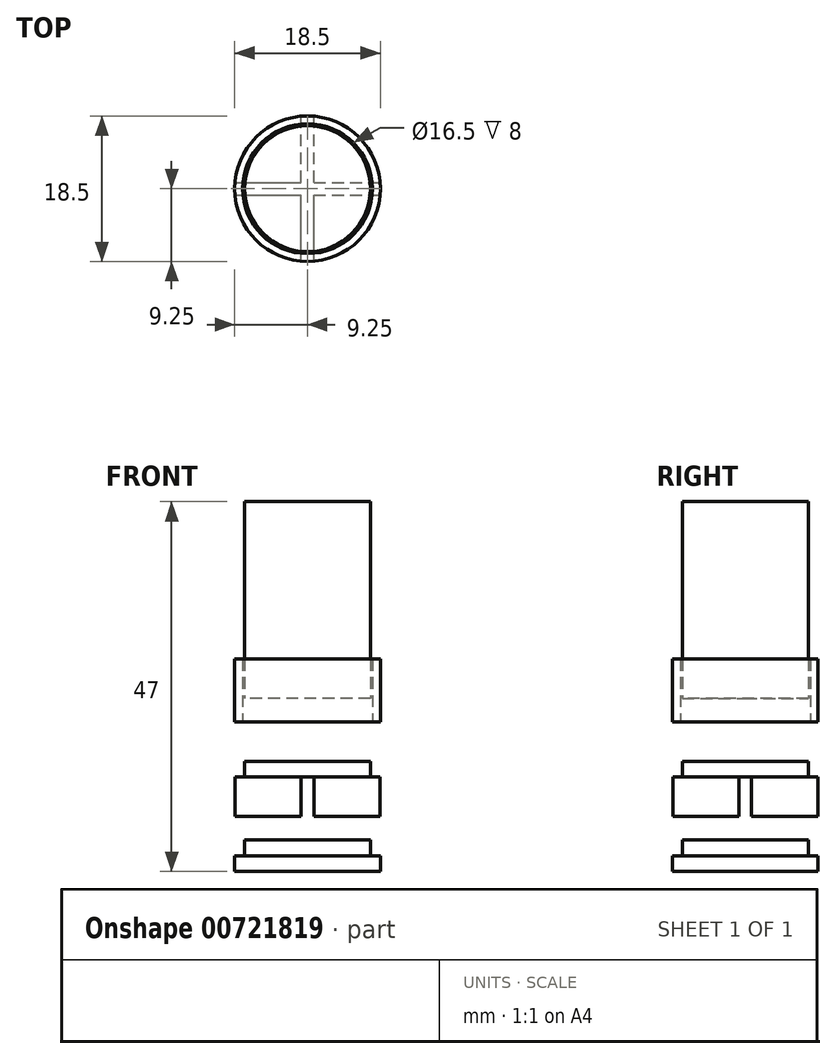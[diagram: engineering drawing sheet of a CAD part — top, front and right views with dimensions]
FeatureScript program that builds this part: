
annotation { "Feature Type Name" : "Feature", "Feature Type Description" : "" }
export const myFeature = defineFeature(function(context is Context, id is Id, definition is map)
    precondition{}
    {
        {
            var Q0;
            Q0=qCreatedBy(makeId("Top.planeOp"),FACE);
            var sketch = newSketch(context, id + "F0", { "sketchPlane" : qUnion([Q0])});
            skCircle(sketch, "E0", {"center": v(0, 0) * mm, "radius": 8 * mm});
            skSolve(sketch);
        }
        {
            var Q0;
            Q0 = qSketchRegion(id + "F0", true);
            extrude(context, id + "F1", {"entities" : qUnion([Q0]), "depth" : 25 * mm, "offsetDistance" : 25 * mm});
        }
        {
            var Q0;
            Q0=qCreatedBy(makeId("Top.planeOp"),FACE);
            var sketch = newSketch(context, id + "F2", { "sketchPlane" : qUnion([Q0])});
            skCircle(sketch, "E1", {"center": v(0, 0) * mm, "radius": 8.25 * mm});
            skCircle(sketch, "E2", {"center": v(0, 0) * mm, "radius": 9.25 * mm});
            skSolve(sketch);
        }
        {
            var Q0;
            Q0 = qSketchRegion(id + "F2", true);
            extrude(context, id + "F3", {"entities" : qUnion([Q0]), "depth" : 5 * mm, "offsetDistance" : 25 * mm, "hasSecondDirection" : true, "secondDirectionOppositeDirection" : true, "secondDirectionDepth" : 3 * mm});
        }
        {
            var Q0;
            Q0=makeQuery(id+"F1.opExtrude","CAP_FACE",FACE,{"disambiguationData":[OSD([sQuery(id+"F0.wireOp",EDGE,"E0")])],"isStart":true});
            cPlane(context, id + "F4", {"entities" : qUnion([Q0]), "cplaneType" : CPlaneType.OFFSET, "offset" : 10 * mm, "width" : 150 * mm, "height" : 150 * mm});
        }
        {
            var Q0;
            Q0=qCreatedBy(id+"F4.planeOp",FACE);
            var sketch = newSketch(context, id + "F5", { "sketchPlane" : qUnion([Q0])});
            skCircle(sketch, "E3", {"center": v(0, 0) * mm, "radius": 8 * mm});
            skCircle(sketch, "E4.0", {"center": v(0, 0) * mm, "radius": 8.25 * mm, "construction": true});
            skSolve(sketch);
        }
        {
            var Q0;
            Q0 = qSketchRegion(id + "F5", true);
            extrude(context, id + "F6", {"entities" : qUnion([Q0]), "oppositeDirection" : true, "depth" : 2 * mm, "offsetDistance" : 25 * mm});
        }
        {
            var Q0;
            Q0=qCreatedBy(id+"F4.planeOp",FACE);
            var sketch = newSketch(context, id + "F7", { "sketchPlane" : qUnion([Q0])});
            skCircle(sketch, "E5.0", {"center": v(0, 0) * mm, "radius": 9.25 * mm});
            skLineSegment(sketch, "E6.bottom", {"start": v(-10.37, 0.8) * mm, "end": v(10.37, 0.8) * mm});
            skLineSegment(sketch, "E6.top", {"start": v(-10.37, -0.8) * mm, "end": v(10.37, -0.8) * mm});
            skLineSegment(sketch, "E6.left", {"start": v(-10.37, 0.8) * mm, "end": v(-10.37, -0.8) * mm});
            skLineSegment(sketch, "E6.right", {"start": v(10.37, 0.8) * mm, "end": v(10.37, -0.8) * mm});
            skLineSegment(sketch, "E7.bottom", {"start": v(-0.8, 10.05) * mm, "end": v(0.8, 10.05) * mm});
            skLineSegment(sketch, "E7.top", {"start": v(-0.8, -10.05) * mm, "end": v(0.8, -10.05) * mm});
            skLineSegment(sketch, "E7.left", {"start": v(-0.8, 10.05) * mm, "end": v(-0.8, -10.05) * mm});
            skLineSegment(sketch, "E7.right", {"start": v(0.8, 10.05) * mm, "end": v(0.8, -10.05) * mm});
            skSolve(sketch);
        }
        {
            var Q0;
            {var subQ0=sQuery(id+"F7.wireOp",EDGE,"E7.left");var subQ1=sQuery(id+"F7.wireOp",EDGE,"E5.0");var subQ2=makeQuery(id+"F7.imprint","INTERSECT",VERTEX,{"disambiguationData":[OD(0.0)],"derivedFrom":[subQ1,subQ0]});Q0=makeQuery(id+"F7.imprint","IMPRINT",FACE,{"disambiguationData":[TD([[makeQuery(id+"F7.imprint","IMPRINT",EDGE,{"disambiguationData":[TD([[subQ2,-1.0]])],"derivedFrom":subQ1}),1.0]])]});}
            var Q1;
            {var subQ0=sQuery(id+"F7.wireOp",EDGE,"E7.right");var subQ1=sQuery(id+"F7.wireOp",EDGE,"E5.0");var subQ2=makeQuery(id+"F7.imprint","INTERSECT",VERTEX,{"disambiguationData":[OD(0.0)],"derivedFrom":[subQ1,subQ0]});Q1=makeQuery(id+"F7.imprint","IMPRINT",FACE,{"disambiguationData":[TD([[makeQuery(id+"F7.imprint","IMPRINT",EDGE,{"disambiguationData":[TD([[subQ2,1.0]])],"derivedFrom":subQ1}),1.0]])]});}
            var Q2;
            {var subQ0=sQuery(id+"F7.wireOp",EDGE,"E6.top");var subQ1=sQuery(id+"F7.wireOp",EDGE,"E5.0");var subQ2=makeQuery(id+"F7.imprint","INTERSECT",VERTEX,{"disambiguationData":[OD(0.0)],"derivedFrom":[subQ1,subQ0]});Q2=makeQuery(id+"F7.imprint","IMPRINT",FACE,{"disambiguationData":[TD([[makeQuery(id+"F7.imprint","IMPRINT",EDGE,{"disambiguationData":[TD([[subQ2,-1.0]])],"derivedFrom":subQ1}),1.0]])]});}
            var Q3;
            {var subQ0=sQuery(id+"F7.wireOp",EDGE,"E7.right");var subQ1=sQuery(id+"F7.wireOp",EDGE,"E5.0");var subQ2=makeQuery(id+"F7.imprint","INTERSECT",VERTEX,{"disambiguationData":[OD(1.0)],"derivedFrom":[subQ1,subQ0]});Q3=makeQuery(id+"F7.imprint","IMPRINT",FACE,{"disambiguationData":[TD([[makeQuery(id+"F7.imprint","IMPRINT",EDGE,{"disambiguationData":[TD([[subQ2,-1.0]])],"derivedFrom":subQ1}),1.0]])]});}
            extrude(context, id + "F8", {"entities" : qUnion([Q0, Q1, Q2, Q3]), "operationType" : NewBodyOperationType.ADD, "depth" : 5 * mm, "offsetDistance" : 25 * mm});
        }
        {
            var Q0;
            Q0=qCreatedBy(makeId("Top.planeOp"),FACE);
            cPlane(context, id + "F9", {"entities" : qUnion([Q0]), "cplaneType" : CPlaneType.OFFSET, "offset" : 20 * mm, "oppositeDirection" : true, "width" : 150 * mm, "height" : 150 * mm});
        }
        {
            var Q0;
            Q0=qCreatedBy(id+"F9.planeOp",FACE);
            var sketch = newSketch(context, id + "F10", { "sketchPlane" : qUnion([Q0])});
            skCircle(sketch, "E8", {"center": v(0, 0) * mm, "radius": 8 * mm});
            skCircle(sketch, "E9.0", {"center": v(0, 0) * mm, "radius": 9.25 * mm});
            skSolve(sketch);
        }
        {
            var Q0;
            Q0=makeQuery(id+"F10.imprint","IMPRINT",FACE,{"disambiguationData":[TD([[makeQuery(id+"F10.imprint","IMPRINT",EDGE,{"derivedFrom":sQuery(id+"F10.wireOp",EDGE,"E8")}),1.0]])]});
            extrude(context, id + "F11", {"entities" : qUnion([Q0]), "depth" : 2 * mm, "offsetDistance" : 25 * mm});
        }
        {
            var Q0;
            Q0=makeQuery(id+"F10.imprint","IMPRINT",FACE,{"disambiguationData":[TD([[makeQuery(id+"F10.imprint","IMPRINT",EDGE,{"derivedFrom":sQuery(id+"F10.wireOp",EDGE,"E8")}),1.0]])]});
            var Q1;
            Q1=makeQuery(id+"F10.imprint","IMPRINT",FACE,{"disambiguationData":[TD([[makeQuery(id+"F10.imprint","IMPRINT",EDGE,{"derivedFrom":sQuery(id+"F10.wireOp",EDGE,"E8")}),-1.0]])]});
            extrude(context, id + "F12", {"entities" : qUnion([Q0, Q1]), "operationType" : NewBodyOperationType.ADD, "oppositeDirection" : true, "depth" : 2 * mm, "offsetDistance" : 25 * mm});
        }
    });
